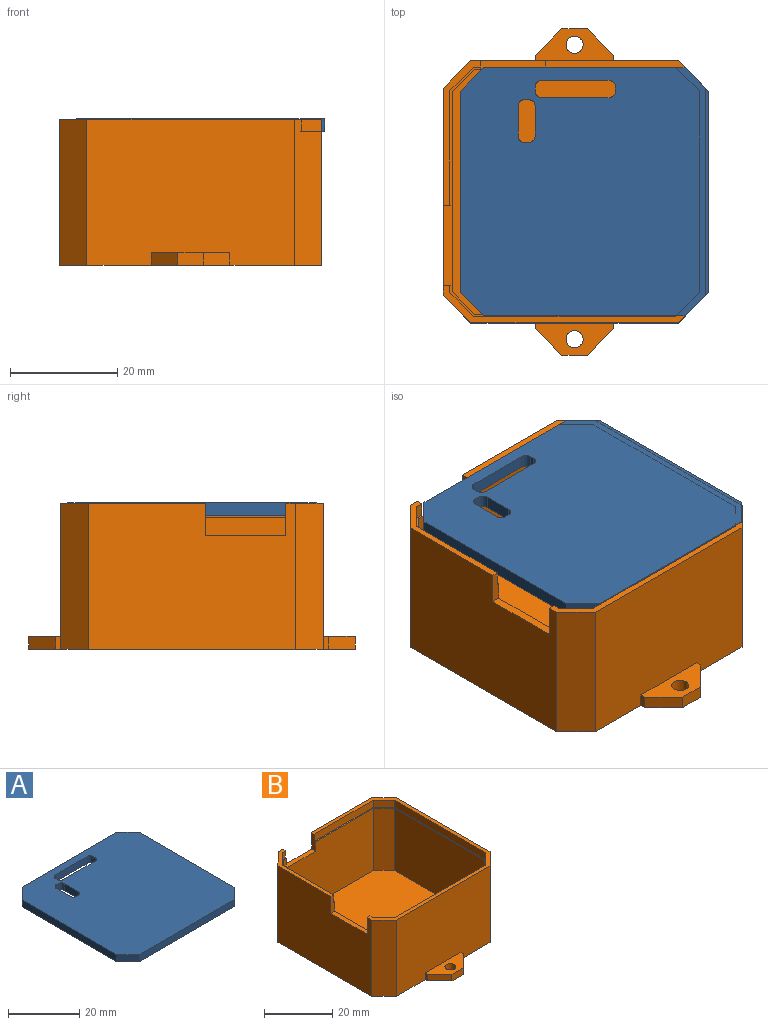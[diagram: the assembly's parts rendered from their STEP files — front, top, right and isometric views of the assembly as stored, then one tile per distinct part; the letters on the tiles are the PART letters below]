
ASSEMBLY  parts=2 mates=1
PART A: 26 faces, bbox 46.4x46.4x2.4 mm
  f0: plane 46.4x46.4mm, normal (0,0,1), area 2043.1mm2, adj f2,f3,f4,f5,f6,f7,f8,f9
  f1: plane 46.4x46.4mm, normal (0,0,-1), area 2043.1mm2, adj f2,f3,f4,f5,f6,f7,f8,f9
  f2: plane 37.6x2.4mm, normal (0,1,0), area 90.2mm2, adj f0,f1,f7,f8
  f3: plane 37.6x2.4mm, normal (-1,0,0), area 90.2mm2, adj f0,f1,f8,f9
  f4: plane 37.6x2.4mm, normal (0,-1,0), area 90.2mm2, adj f0,f1,f6,f9
  f5: plane 37.6x2.4mm, normal (1,0,0), area 90.2mm2, adj f0,f1,f6,f7
  f6: plane 4.4x4.4mm, normal (0.71,-0.71,0), area 14.9mm2, adj f0,f1,f4,f5
  f7: plane 4.4x4.4mm, normal (0.71,0.71,0), area 14.9mm2, adj f0,f1,f2,f5
  f8: plane 4.4x4.4mm, normal (-0.71,0.71,0), area 14.9mm2, adj f0,f1,f2,f3
  f9: plane 4.4x4.4mm, normal (-0.71,-0.71,0), area 14.9mm2, adj f0,f1,f3,f4
  f10: plane 12.6x2.4mm, normal (0,-1,0), area 30.2mm2, adj f0,f1,f22,f25
  f11: plane 2.4x0.8mm, normal (1,0,0), area 1.9mm2, adj f0,f1,f22,f23
  f12: plane 12.6x2.4mm, normal (0,1,0), area 30.2mm2, adj f0,f1,f23,f24
  f13: plane 2.4x0.8mm, normal (-1,0,0), area 1.9mm2, adj f0,f1,f24,f25
  f14: plane 2.4x0.8mm, normal (0,-1,0), area 1.9mm2, adj f0,f1,f18,f21
  f15: plane 5.6x2.4mm, normal (1,0,0), area 13.4mm2, adj f0,f1,f18,f19
  f16: plane 2.4x0.8mm, normal (0,1,0), area 1.9mm2, adj f0,f1,f19,f20
  f17: plane 5.6x2.4mm, normal (-1,0,0), area 13.4mm2, adj f0,f1,f20,f21
  f18: cylinder r=1.2mm len=2.4mm, axis (0,0,1), area 4.5mm2, adj f0,f1,f14,f15
  f19: cylinder r=1.2mm len=2.4mm, axis (0,0,-1), area 4.5mm2, adj f0,f1,f15,f16
  f20: cylinder r=1.2mm len=2.4mm, axis (0,0,1), area 4.5mm2, adj f0,f1,f16,f17
  f21: cylinder r=1.2mm len=2.4mm, axis (0,0,-1), area 4.5mm2, adj f0,f1,f14,f17
  f22: cylinder r=1.2mm len=2.4mm, axis (0,0,1), area 4.5mm2, adj f0,f1,f10,f11
  f23: cylinder r=1.2mm len=2.4mm, axis (0,0,-1), area 4.5mm2, adj f0,f1,f11,f12
  f24: cylinder r=1.2mm len=2.4mm, axis (0,0,1), area 4.5mm2, adj f0,f1,f12,f13
  f25: cylinder r=1.2mm len=2.4mm, axis (0,0,-1), area 4.5mm2, adj f0,f1,f10,f13
PART B: 52 faces, bbox 49x61x27.3 mm
  f0: plane 38.73x27.3mm, normal (0,1,0), area 949.9mm2, adj f20,f24,f25,f26,f27,f31,f32,f33
  f1: plane 46.6x46.6mm, normal (0,0,1), area 47.6mm2, adj f2,f3,f4,f5,f9,f10,f11,f12
  f2: plane 37.73x2.6mm, normal (-1,0,0), area 98.1mm2, adj f1,f24,f36,f37
  f3: plane 24.37x2.6mm, normal (0,-1,0), area 63.4mm2, adj f1,f24,f31,f37
  f4: plane 37.73x2.6mm, normal (0,1,0), area 98.1mm2, adj f1,f24,f35,f36
  f5: plane 2.6x1.37mm, normal (1,0,0), area 3.6mm2, adj f1,f24,f28,f35
  f6: plane 2.6x1.37mm, normal (0,-1,0), area 3.6mm2, adj f8,f26,f33,f34
  f7: plane 21.37x2.6mm, normal (1,0,0), area 55.6mm2, adj f8,f26,f29,f34
  f8: plane 25.8x5.8mm, normal (0,0,1), area 11.5mm2, adj f6,f7,f9,f10,f16,f29,f33,f34
  f9: plane 37.4x22.3mm, normal (0,-1,0), area 793.2mm2, adj f1,f8,f15,f16,f17,f31,f32,f33
  f10: plane 37.4x22.3mm, normal (1,0,0), area 783mm2, adj f1,f8,f14,f16,f17,f28,f29,f30
  f11: plane 37.4x22.3mm, normal (-1,0,0), area 834mm2, adj f1,f13,f15,f17
  f12: plane 37.4x22.3mm, normal (0,1,0), area 834mm2, adj f1,f13,f14,f17
  f13: plane 22.3x4.2mm, normal (-0.71,0.71,0), area 132.5mm2, adj f1,f11,f12,f17
  f14: plane 22.3x4.2mm, normal (0.71,0.71,0), area 132.5mm2, adj f1,f10,f12,f17
  f15: plane 22.3x4.2mm, normal (-0.71,-0.71,0), area 132.5mm2, adj f1,f9,f11,f17
  f16: plane 22.3x4.2mm, normal (0.71,-0.71,0), area 132.5mm2, adj f8,f9,f10,f17
  f17: plane 45.8x45.8mm, normal (0,0,1), area 2062.4mm2, adj f9,f10,f11,f12,f13,f14,f15,f16
  f18: plane 38.73x27.3mm, normal (1,0,0), area 1057.2mm2, adj f20,f23,f24,f27
  f19: plane 38.73x27.3mm, normal (0,-1,0), area 1021.9mm2, adj f20,f22,f23,f24,f38,f39,f40
  f20: plane 61x49mm, normal (0,0,-1), area 2458.8mm2, adj f0,f18,f19,f21,f22,f23,f25,f27
  f21: plane 38.73x27.3mm, normal (-1,0,0), area 967.2mm2, adj f20,f22,f24,f25,f26,f28,f29,f30
  f22: plane 27.3x5.14mm, normal (-0.71,-0.71,0), area 198.3mm2, adj f19,f20,f21,f24
  f23: plane 27.3x5.14mm, normal (0.71,-0.71,0), area 198.3mm2, adj f18,f19,f20,f24
  f24: plane 49x49mm, normal (0,0,1), area 147.6mm2, adj f0,f2,f3,f4,f5,f18,f19,f21
  f25: plane 27.3x5.14mm, normal (-0.71,0.71,0), area 198.3mm2, adj f0,f20,f21,f26
  f26: plane 27x7mm, normal (0,0,1), area 36mm2, adj f0,f6,f7,f21,f25,f29,f33,f34
  f27: plane 27.3x5.14mm, normal (0.71,0.71,0), area 198.3mm2, adj f0,f18,f20,f24
  f28: plane 6x1.6mm, normal (0,1,0), area 8.6mm2, adj f1,f5,f10,f21,f24,f30
  f29: plane 6x1.6mm, normal (0,-1,0), area 8.6mm2, adj f7,f8,f10,f21,f26,f30
  f30: plane 15x1.6mm, normal (0,0,1), area 24mm2, adj f10,f21,f28,f29
  f31: plane 6x1.6mm, normal (-1,0,0), area 8.6mm2, adj f0,f1,f3,f9,f24,f32
  f32: plane 12x1.6mm, normal (0,0,1), area 19.2mm2, adj f0,f9,f31,f33
  f33: plane 6x1.6mm, normal (1,0,0), area 8.6mm2, adj f0,f6,f8,f9,f26,f32
  f34: plane 4.43x4.43mm, normal (0.71,-0.71,0), area 16.3mm2, adj f6,f7,f8,f26
  f35: plane 4.43x4.43mm, normal (0.71,0.71,0), area 16.3mm2, adj f1,f4,f5,f24
  f36: plane 4.43x4.43mm, normal (-0.71,0.71,0), area 16.3mm2, adj f1,f2,f4,f24
  f37: plane 4.43x4.43mm, normal (-0.71,-0.71,0), area 16.3mm2, adj f1,f2,f3,f24
  f38: plane 2.4x1mm, normal (-1,0,0), area 2.4mm2, adj f19,f20,f40,f51
  f39: plane 2.4x1mm, normal (1,0,0), area 2.4mm2, adj f19,f20,f40,f50
  f40: plane 14.73x6mm, normal (0,0,1), area 55.3mm2, adj f19,f38,f39,f41,f46,f50,f51
  f41: plane 4.73x2.4mm, normal (0,-1,0), area 11.3mm2, adj f20,f40,f50,f51
  f42: plane 2.4x1mm, normal (-1,0,0), area 2.4mm2, adj f0,f20,f43,f48
  f43: plane 14.73x6mm, normal (0,0,1), area 55.3mm2, adj f0,f42,f44,f45,f47,f48,f49
  f44: plane 2.4x1mm, normal (1,0,0), area 2.4mm2, adj f0,f20,f43,f49
  f45: plane 4.73x2.4mm, normal (0,1,0), area 11.3mm2, adj f20,f43,f48,f49
  f46: cylinder r=1.6mm len=3.2mm, axis (0,0,1), area 24.1mm2, adj f20,f40
  f47: cylinder r=1.6mm len=3.2mm, axis (0,0,1), area 24.1mm2, adj f20,f43
  f48: plane 5x5mm, normal (-0.71,0.71,0), area 17mm2, adj f20,f42,f43,f45
  f49: plane 5x5mm, normal (0.71,0.71,0), area 17mm2, adj f20,f43,f44,f45
  f50: plane 5x5mm, normal (0.71,-0.71,0), area 17mm2, adj f20,f39,f40,f41
  f51: plane 5x5mm, normal (-0.71,-0.71,0), area 17mm2, adj f20,f38,f40,f41
PLACE A t=(-73.7,-3.16,25)mm
PLACE B at identity fixed
MATE slider B.f17 <-> A.f0  axis (0,0,1) through (-41.84,40.26,2.4)mm
